# Revit family: Haworth_VSeries_StorageTower_5High
name_source: partatom
category: Furniture Systems
revit_build: Autodesk Revit 2018 (Build: 20170223_1515(x64)
units: mm (PartAtom-declared; Revit-internal decimal feet)

## family parameters
Always vertical = Yes
Cut with Voids When Loaded = No
OmniClass Number = 23.40.70.14.64.21
OmniClass Title = Systems Furniture
Part Type = Normal
Room Calculation Point = No
Round Connector Dimension = Use Diameter
Shared = No
Work Plane-Based = No

## types (4) — shared parameters
Actual Depth = 23"
Actual Height = 63 1/2"
Actual Width = 24"
Assembly Code = E2020200
Cabinet Finish = Haworth _ Paint _ Metallic Champagne
Cabinet Height = 27 1/2"
Description = Haworth - VSeries Storage Tower - 5 High
Door Finish = Haworth _ Paint _ Metallic Champagne
Door Height = 59 123/128"
Door Height 2 = 34 1/2"
Door Width = 9"
Drawer 1 Height = 11 15/16"
Drawer 3 Full Pull = No
Drawer 3 Height = 5 15/16"
Drawer Finish = Haworth _ Paint _ Metallic Champagne
Drawer Width = 14 7/8"
Full Pull = No
Manufacturer = Haworth
Max. Height = 63 1/2"
Max. Width = 47 7/8"
Min. Height = 27 1/2"
Min. Width = 29 7/8"
Model = Haworth - VSeries Storage Tower - 5 High
Pull Finish = Haworth _ Polymer _ Gray Tone
Pull Height Centerline = 42 91/128"
Pull Height Centerline 2 = 17 1/4"
Revision Number = 2
Shelf Depth = 13 1/2"
Shelf Finish = Haworth _ Paint _ Metallic Champagne
Shelf Width = 21 1/2"
Size = Verify Final Dim. w/ Haworth
Standard Pull = Yes
Storage Full Pull = No
Sustainability Info = http://www.haworth.com
Top Height = 36"
URL = www.haworth.com
URL - Product = http://www.haworth.com
Warranty = http://www.haworth.com

## per-type parameters (varying)
| type | Box Box File | Drawer 2 Height | Drawer 3 | Drawer 3 Standard Pull | File File | Storage Standard Pull | Upper Bookcase | Upper Door |
| Box Box File - Upper Bookcase | Yes | 5 15/16" | Yes | Yes | No | No | Yes | No |
| Box Box File - Upper Door | Yes | 5 15/16" | Yes | Yes | No | Yes | No | Yes |
| File File - Upper Bookcase | No | 11 15/16" | No | No | Yes | No | Yes | No |
| File File - Upper Door | No | 11 15/16" | No | No | Yes | Yes | No | Yes |

## geometry (parser evidence)
native form markers: Sweep x13
no freeform markers — native parametric forms only
